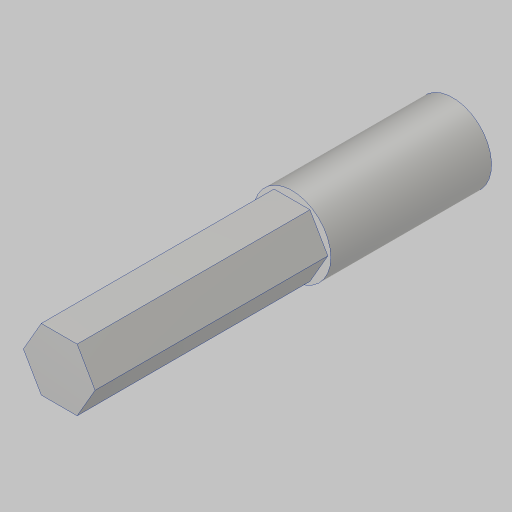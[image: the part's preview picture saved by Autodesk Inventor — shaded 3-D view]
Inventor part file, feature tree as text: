
AUTODESK INVENTOR PART (.ipt)
format: ipt  version: 2023.5 (Build 275446000, 446)  size: 139,264 bytes
history: native  units: in
note: dims shown in document units (in); Inventor stores cm internally (conversion verified against a paired STEP export)
features: extrude x4, sketch x4, projected_geometry x4
ambient origin geometry x8: Origin, YZ Plane, XZ Plane, XY Plane, X Axis, Y Axis, Z Axis, Center Point
bodies: Solid1 (feature_tree)
feature tree (12):
  extrude  "Extrusion1"  Depth=3.5625in TaperAngle=0.0deg
  extrude  "Extrusion2"  Depth=0.5in TaperAngle=0.0deg
  extrude  "Extrusion3"  Depth=0.5in TaperAngle=0.0deg
  extrude  "Extrusion6"  TaperAngle=0.0deg  [1 undecoded]
  sketch  "Sketch1"  dims[d0=0.625in d1=3.5625in d2=0.0in]
  sketch  "Sketch2"  dims[d3=0.5in d4=2.125in d5=0.0in]
  projected_geometry  "Projected Loop1"
  sketch  "Sketch3"  dims[d6=0.5in d7=0.25in d8=0.0in]
  projected_geometry  "Projected Loop2"
  sketch  "Sketch6"  dims[d15=3.17in d16=0.0in d17=0.0in]
  projected_geometry  "Project Cut Edges3"
  projected_geometry  "Project Cut Edges4"
note: 1 required parameter value undecoded (feature->parameter linkage not recoverable at this tier; creation-order binding heuristic only, values carry confidence <= 0.55)
